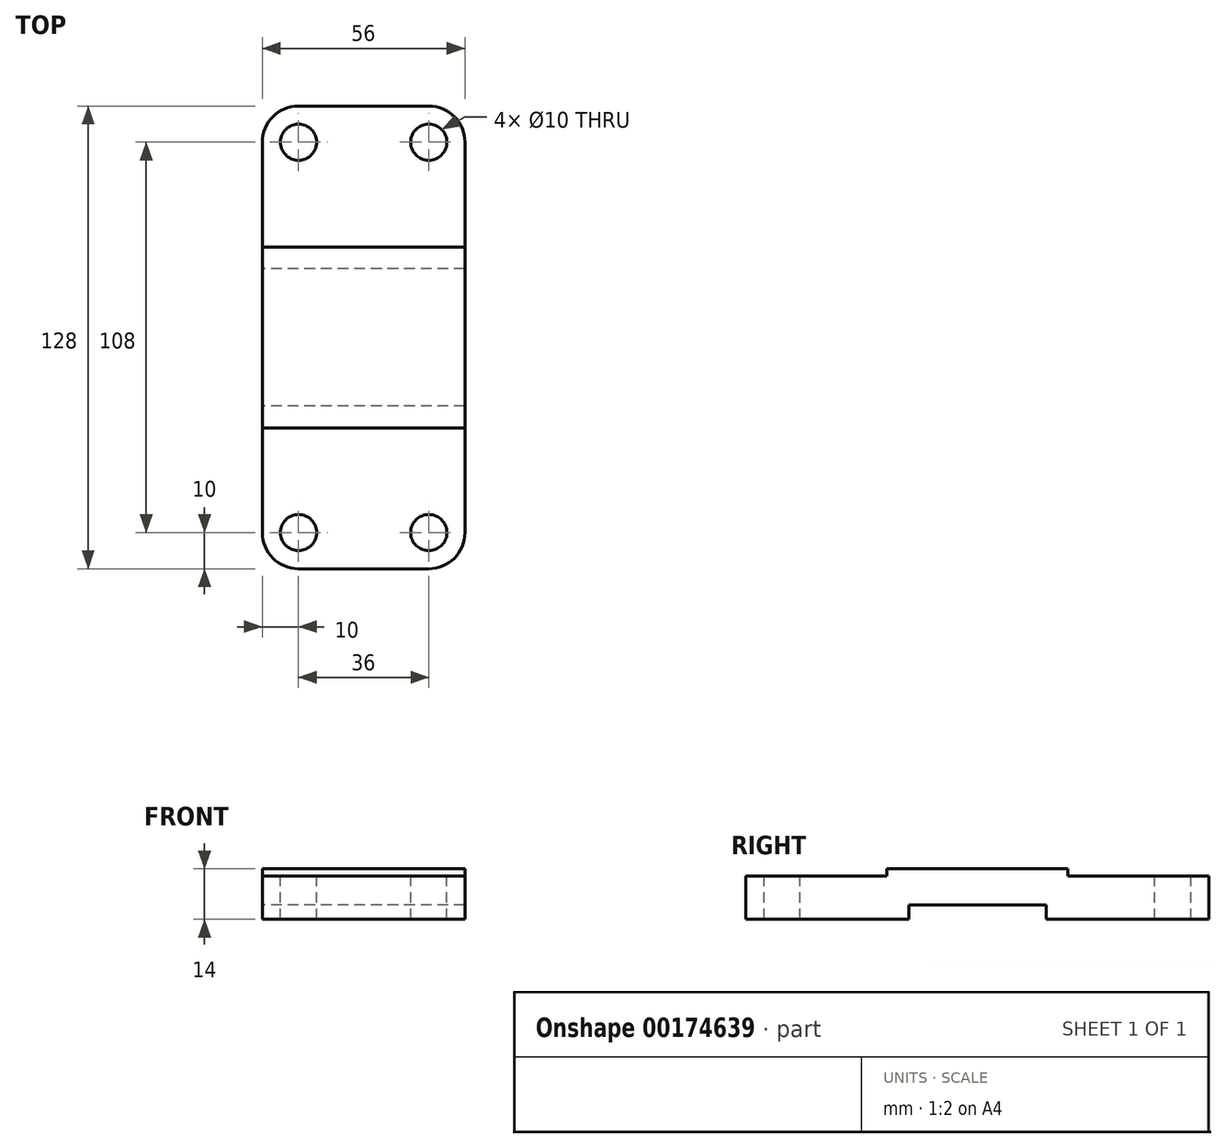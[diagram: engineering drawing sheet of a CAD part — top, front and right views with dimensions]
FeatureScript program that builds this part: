
annotation { "Feature Type Name" : "Feature", "Feature Type Description" : "" }
export const myFeature = defineFeature(function(context is Context, id is Id, definition is map)
    precondition{}
    {
        {
            var Q0;
            Q0=qCreatedBy(makeId("Right.planeOp"),FACE);
            var sketch = newSketch(context, id + "F0", { "sketchPlane" : qUnion([Q0])});
            skLineSegment(sketch, "E0", {"start": v(0, 0) * mm, "end": v(0, 82.73) * mm, "construction": true});
            skLineSegment(sketch, "E1.bottom", {"start": v(-64, -7) * mm, "end": v(-19, -7) * mm});
            skLineSegment(sketch, "E1.top", {"start": v(-25, 7) * mm, "end": v(25, 7) * mm});
            skLineSegment(sketch, "E1.left", {"start": v(-64, -7) * mm, "end": v(-64, 5) * mm});
            skLineSegment(sketch, "E1.right", {"start": v(64, -7) * mm, "end": v(64, 5) * mm});
            skPoint(sketch, "E1.middle", {"position": v(0, 0) * mm});
            skLineSegment(sketch, "E2", {"start": v(-64, 5) * mm, "end": v(-25, 5) * mm});
            skLineSegment(sketch, "E3", {"start": v(-25, 5) * mm, "end": v(-25, 7) * mm});
            skLineSegment(sketch, "E4", {"start": v(25, 7) * mm, "end": v(25, 5) * mm});
            skLineSegment(sketch, "E5", {"start": v(25, 5) * mm, "end": v(64, 5) * mm});
            skPoint(sketch, "E6.orphan", {"position": v(-64, 7) * mm});
            skPoint(sketch, "E7.orphan", {"position": v(64, 7) * mm});
            skLineSegment(sketch, "E8", {"start": v(-19, -7) * mm, "end": v(-19, -3) * mm});
            skLineSegment(sketch, "E9", {"start": v(-19, -3) * mm, "end": v(19, -3) * mm});
            skLineSegment(sketch, "E10", {"start": v(19, -3) * mm, "end": v(19, -7) * mm});
            skLineSegment(sketch, "E11.trimOffspring", {"start": v(19, -7) * mm, "end": v(64, -7) * mm});
            skSolve(sketch);
        }
        {
            var Q0;
            Q0=makeQuery(id+"F0.imprint","IMPRINT",FACE,{"disambiguationData":[TD([[makeQuery(id+"F0.imprint","IMPRINT",EDGE,{"derivedFrom":sQuery(id+"F0.wireOp",EDGE,"E1.bottom")}),1.0]])]});
            extrude(context, id + "F1", {"entities" : qUnion([Q0]), "depth" : 56 * mm, "symmetric" : true});
        }
        {
            var Q0;
            Q0=makeQuery(id+"F1.opExtrude","CAP_EDGE",EDGE,{"disambiguationData":[OSD([sQuery(id+"F0.wireOp",EDGE,"E1.left")])],"isStart":false});
            var Q1;
            Q1=makeQuery(id+"F1.opExtrude","CAP_EDGE",EDGE,{"disambiguationData":[OSD([sQuery(id+"F0.wireOp",EDGE,"E1.left")])],"isStart":true});
            var Q2;
            Q2=makeQuery(id+"F1.opExtrude","CAP_EDGE",EDGE,{"disambiguationData":[OSD([sQuery(id+"F0.wireOp",EDGE,"E1.right")])],"isStart":false});
            var Q3;
            Q3=makeQuery(id+"F1.opExtrude","CAP_EDGE",EDGE,{"disambiguationData":[OSD([sQuery(id+"F0.wireOp",EDGE,"E1.right")])],"isStart":true});
            fillet(context, id + "F2", {"entities" : qUnion([Q0, Q1, Q2, Q3]), "radius" : 10 * mm, "tangentPropagation" : true, "allowEdgeOverflow" : false});
        }
        {
            var Q0;
            Q0=makeQuery(id+"F1.opExtrude","SWEPT_FACE",FACE,{"disambiguationData":[OSD([sQuery(id+"F0.wireOp",EDGE,"E2")])]});
            var sketch = newSketch(context, id + "F3", { "sketchPlane" : qUnion([Q0])});
            skCircle(sketch, "E12", {"center": v(-18, -54) * mm, "radius": 5 * mm});
            skLineSegment(sketch, "E13", {"start": v(0, 0) * mm, "end": v(-44.05, 0) * mm, "construction": true});
            skLineSegment(sketch, "E14", {"start": v(0, 0) * mm, "end": v(0, 43.97) * mm, "construction": true});
            skCircle(sketch, "E15.MirrorC", {"center": v(-18, 54) * mm, "radius": 5 * mm});
            skCircle(sketch, "E16.MirrorC", {"center": v(18, 54) * mm, "radius": 5 * mm});
            skCircle(sketch, "E17.MirrorC", {"center": v(18, -54) * mm, "radius": 5 * mm});
            skSolve(sketch);
        }
        {
            var Q0;
            Q0 = qSketchRegion(id + "F3", true);
            extrude(context, id + "F4", {"entities" : qUnion([Q0]), "operationType" : NewBodyOperationType.REMOVE, "endBound" : BoundingType.THROUGH_ALL, "oppositeDirection" : true, "depth" : 25 * mm});
        }
    });
